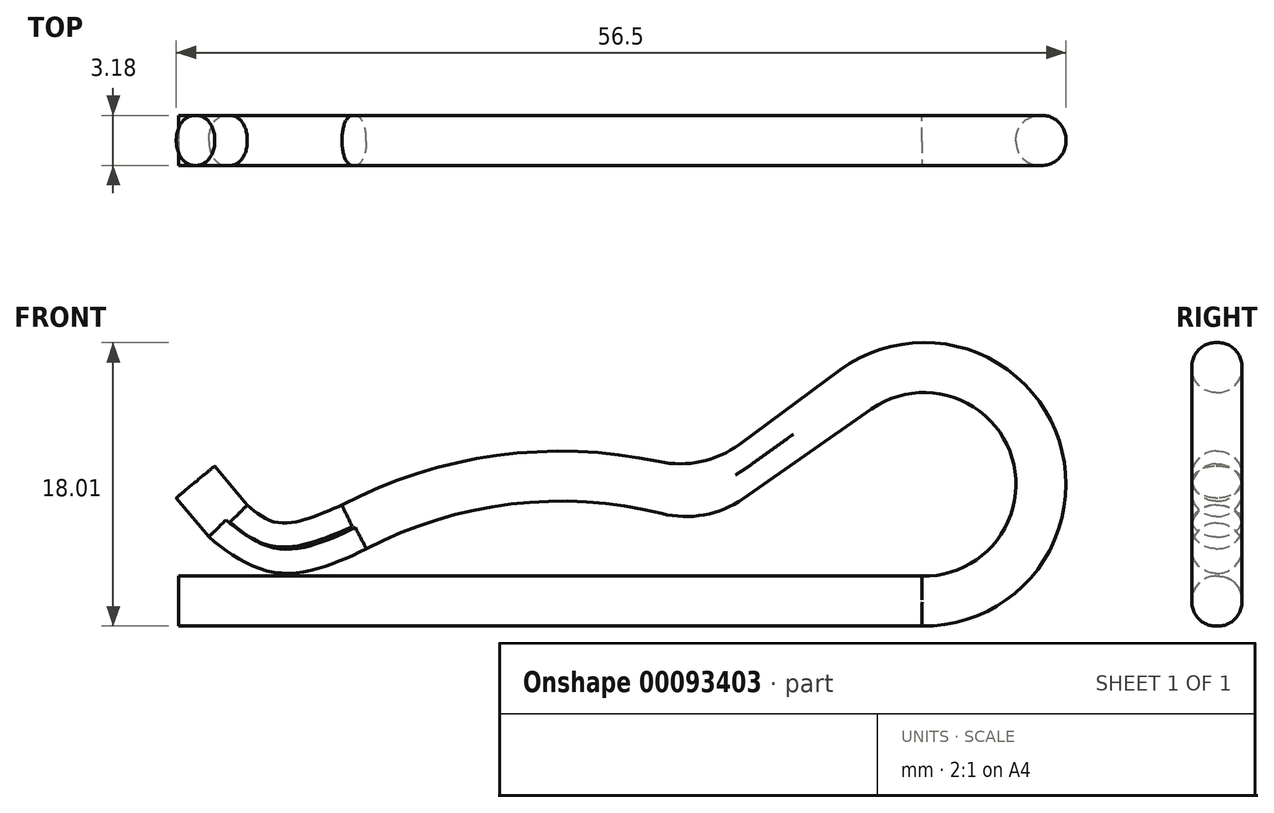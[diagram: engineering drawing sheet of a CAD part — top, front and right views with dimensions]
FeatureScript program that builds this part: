
annotation { "Feature Type Name" : "Feature", "Feature Type Description" : "" }
export const myFeature = defineFeature(function(context is Context, id is Id, definition is map)
    precondition{}
    {
        {
            var Q0;
            Q0=qCreatedBy(makeId("Front.planeOp"),FACE);
            var sketch = newSketch(context, id + "F0", { "sketchPlane" : qUnion([Q0])});
            skLineSegment(sketch, "E0.bottom", {"start": v(0, -36.18) * mm, "end": v(-24.24, -36.18) * mm});
            skLineSegment(sketch, "E0.top", {"start": v(0, -39.36) * mm, "end": v(-24.24, -39.36) * mm});
            skLineSegment(sketch, "E0.right", {"start": v(-24.24, -36.18) * mm, "end": v(-24.24, -39.36) * mm});
            skLineSegment(sketch, "E1.bottom", {"start": v(0, -39.36) * mm, "end": v(22.96, -39.36) * mm});
            skLineSegment(sketch, "E1.top", {"start": v(0, -36.18) * mm, "end": v(22.96, -36.18) * mm});
            skLineSegment(sketch, "E1.right", {"start": v(22.96, -39.36) * mm, "end": v(22.96, -39.03) * mm});
            skArc(sketch, "E2", {"start": v(22.96, -36.18) * mm, "mid": v(28.68, -28.67) * mm, "end": v(19.76, -25.57) * mm});
            skPoint(sketch, "E2.second.point", {"position": v(22.96, -24.52) * mm});
            skPoint(sketch, "E2.third.point", {"position": v(28.93, -30.28) * mm});
            skArc(sketch, "E3", {"start": v(6.44, -32.21) * mm, "mid": v(-3.15, -31.6) * mm, "end": v(-12.33, -34.45) * mm});
            skArc(sketch, "E4", {"start": v(6.26, -28.91) * mm, "mid": v(-4.05, -28.52) * mm, "end": v(-13.88, -31.67) * mm});
            skLineSegment(sketch, "E5", {"start": v(-22.33, -33.7) * mm, "end": v(-24.4, -31.21) * mm});
            skLineSegment(sketch, "E6", {"start": v(-24.4, -31.21) * mm, "end": v(-21.96, -29.19) * mm});
            skLineSegment(sketch, "E7", {"start": v(-21.96, -29.19) * mm, "end": v(-19.9, -31.67) * mm});
            skLineSegment(sketch, "E8", {"start": v(17.76, -23.1) * mm, "end": v(11.36, -27.81) * mm});
            skLineSegment(sketch, "E9", {"start": v(19.76, -25.57) * mm, "end": v(11.61, -31.26) * mm});
            skArc(sketch, "E10.trimOffspring", {"start": v(22.96, -39.36) * mm, "mid": v(31.67, -27.6) * mm, "end": v(17.76, -23.1) * mm});
            skArc(sketch, "E11.trimOffspring", {"start": v(23.23, -39.36) * mm, "mid": v(23.1, -39.2) * mm, "end": v(22.96, -39.03) * mm});
            skPoint(sketch, "E12.center.orphan", {"position": v(0, -31.42) * mm});
            skFitSpline(sketch, "E13", {"points": [v(-22.33, -33.7) * mm, v(-17.91, -35.98) * mm, v(-12.33, -34.45) * mm], "startDerivative": vector(8.8, -7.3) * mm, "endDerivative": vector(11.19, 5.62) * mm});
            skPoint(sketch, "E14.2.internal.snap0", {"position": v(-19.9, -31.67) * mm});
            skFitSpline(sketch, "E14", {"points": [v(-19.9, -31.67) * mm, v(-17.87, -32.8) * mm, v(-13.88, -31.67) * mm], "startDerivative": vector(4.25, -3.62) * mm, "endDerivative": vector(7.61, 3.29) * mm});
            skPoint(sketch, "E15.orphan", {"position": v(-17.83, -34.15) * mm});
            skPoint(sketch, "E16.orphan", {"position": v(-20.27, -36.18) * mm});
            skPoint(sketch, "E17.visualSharp", {"position": v(8.92, -29.61) * mm});
            skArc(sketch, "E17.filletArc", {"start": v(6.26, -28.91) * mm, "mid": v(8.93, -28.91) * mm, "end": v(11.36, -27.81) * mm});
            skPoint(sketch, "E18.visualSharp", {"position": v(9.09, -33.02) * mm});
            skArc(sketch, "E18.filletArc", {"start": v(6.44, -32.21) * mm, "mid": v(9.13, -32.3) * mm, "end": v(11.61, -31.26) * mm});
            skSolve(sketch);
        }
        {
            var Q0;
            Q0 = qSketchRegion(id + "F0", true);
            extrude(context, id + "F1", {"entities" : qUnion([Q0]), "depth" : 3.17 * mm, "offsetDistance" : 25.4 * mm});
        }
        {
            var Q0;
            Q0=makeQuery(id+"F1.opExtrude","CAP_EDGE",EDGE,{"disambiguationData":[OSD([sQuery(id+"F0.wireOp",EDGE,"E13")])],"isStart":false});
            var Q1;
            Q1=makeQuery(id+"F1.opExtrude","CAP_EDGE",EDGE,{"disambiguationData":[OSD([sQuery(id+"F0.wireOp",EDGE,"E9")])],"isStart":false});
            var Q2;
            Q2=makeQuery(id+"F1.opExtrude","CAP_EDGE",EDGE,{"disambiguationData":[OSD([sQuery(id+"F0.wireOp",EDGE,"E0.bottom"),sQuery(id+"F0.wireOp",EDGE,"E1.top")])],"isStart":false});
            var Q3;
            Q3=makeQuery(id+"F1.opExtrude","CAP_EDGE",EDGE,{"disambiguationData":[OSD([sQuery(id+"F0.wireOp",EDGE,"E2")])],"isStart":false});
            var Q4;
            Q4=makeQuery(id+"F1.opExtrude","CAP_EDGE",EDGE,{"disambiguationData":[OSD([sQuery(id+"F0.wireOp",EDGE,"E0.top"),sQuery(id+"F0.wireOp",EDGE,"E1.bottom")])],"isStart":false});
            var Q5;
            Q5=makeQuery(id+"F1.opExtrude","CAP_EDGE",EDGE,{"disambiguationData":[OSD([sQuery(id+"F0.wireOp",EDGE,"E10.trimOffspring")])],"isStart":false});
            var Q6;
            Q6=makeQuery(id+"F1.opExtrude","CAP_EDGE",EDGE,{"disambiguationData":[OSD([sQuery(id+"F0.wireOp",EDGE,"E7")])],"isStart":false});
            var Q7;
            Q7=makeQuery(id+"F1.opExtrude","CAP_EDGE",EDGE,{"disambiguationData":[OSD([sQuery(id+"F0.wireOp",EDGE,"E0.bottom"),sQuery(id+"F0.wireOp",EDGE,"E1.top")])],"isStart":true});
            var Q8;
            Q8=makeQuery(id+"F1.opExtrude","CAP_EDGE",EDGE,{"disambiguationData":[OSD([sQuery(id+"F0.wireOp",EDGE,"E0.top"),sQuery(id+"F0.wireOp",EDGE,"E1.bottom")])],"isStart":true});
            var Q9;
            Q9=makeQuery(id+"F1.opExtrude","CAP_EDGE",EDGE,{"disambiguationData":[OSD([sQuery(id+"F0.wireOp",EDGE,"E10.trimOffspring")])],"isStart":true});
            var Q10;
            Q10=makeQuery(id+"F1.opExtrude","CAP_EDGE",EDGE,{"disambiguationData":[OSD([sQuery(id+"F0.wireOp",EDGE,"E9")])],"isStart":true});
            var Q11;
            Q11=makeQuery(id+"F1.opExtrude","CAP_EDGE",EDGE,{"disambiguationData":[OSD([sQuery(id+"F0.wireOp",EDGE,"E13")])],"isStart":true});
            var Q12;
            Q12=makeQuery(id+"F1.opExtrude","CAP_EDGE",EDGE,{"disambiguationData":[OSD([sQuery(id+"F0.wireOp",EDGE,"E7")])],"isStart":true});
            var Q13;
            Q13=makeQuery(id+"F1.opExtrude","CAP_EDGE",EDGE,{"disambiguationData":[OSD([sQuery(id+"F0.wireOp",EDGE,"E5")])],"isStart":true});
            var Q14;
            Q14=makeQuery(id+"F1.opExtrude","CAP_EDGE",EDGE,{"disambiguationData":[OSD([sQuery(id+"F0.wireOp",EDGE,"E5")])],"isStart":false});
            fillet(context, id + "F2", {"entities" : qUnion([Q0, Q1, Q2, Q3, Q4, Q5, Q6, Q7, Q8, Q9, Q10, Q11, Q12, Q13, Q14]), "radius" : 1.52 * mm, "tangentPropagation" : true, "allowEdgeOverflow" : false});
        }
    });
